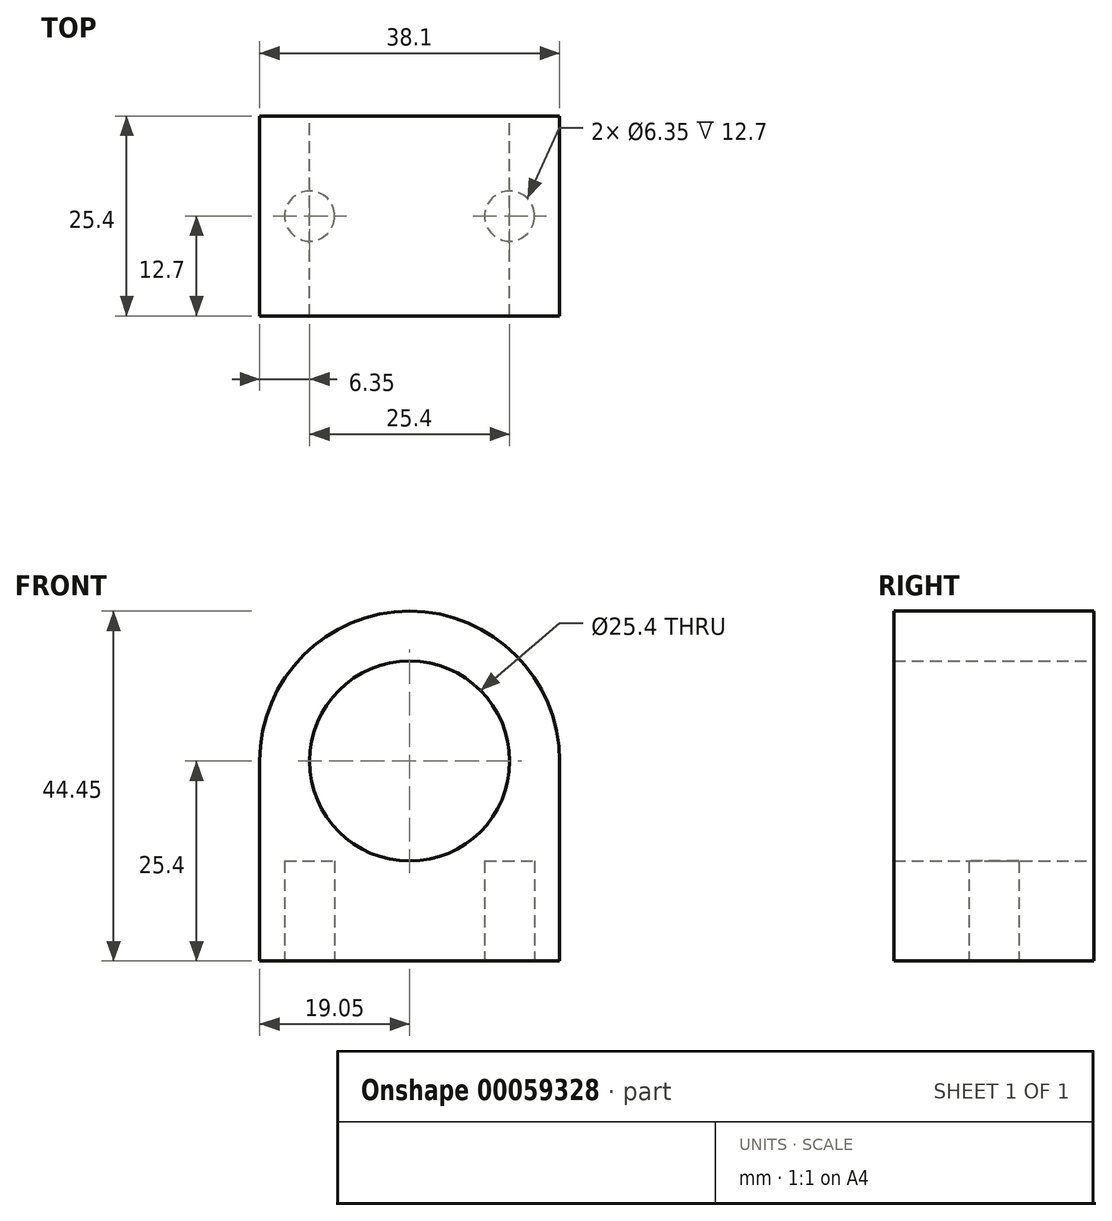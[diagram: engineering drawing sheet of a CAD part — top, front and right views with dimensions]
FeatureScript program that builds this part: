
annotation { "Feature Type Name" : "Feature", "Feature Type Description" : "" }
export const myFeature = defineFeature(function(context is Context, id is Id, definition is map)
    precondition{}
    {
        {
            var Q0;
            Q0=qCreatedBy(makeId("Front.planeOp"),FACE);
            var sketch = newSketch(context, id + "F0", { "sketchPlane" : qUnion([Q0])});
            skArc(sketch, "E0", {"start": v(19.05, 0) * mm, "mid": v(0, 19.05) * mm, "end": v(-19.05, 0) * mm});
            skLineSegment(sketch, "E1.top", {"start": v(-19.05, -25.4) * mm, "end": v(19.05, -25.4) * mm});
            skLineSegment(sketch, "E1.left", {"start": v(-19.05, 0) * mm, "end": v(-19.05, -25.4) * mm});
            skLineSegment(sketch, "E1.right", {"start": v(19.05, 0) * mm, "end": v(19.05, -25.4) * mm});
            skCircle(sketch, "E2", {"center": v(0, 0) * mm, "radius": 12.7 * mm});
            skSolve(sketch);
        }
        {
            var Q0;
            Q0=makeQuery(id+"F0.imprint","IMPRINT",FACE,{"disambiguationData":[TD([[makeQuery(id+"F0.imprint","IMPRINT",EDGE,{"derivedFrom":sQuery(id+"F0.wireOp",EDGE,"E0")}),1.0]])]});
            extrude(context, id + "F1", {"entities" : qUnion([Q0]), "depth" : 25.4 * mm});
        }
        {
            var Q0;
            Q0=makeQuery(id+"F1.opExtrude","SWEPT_FACE",FACE,{"disambiguationData":[OSD([sQuery(id+"F0.wireOp",EDGE,"E1.top")])]});
            var sketch = newSketch(context, id + "F2", { "sketchPlane" : qUnion([Q0])});
            skCircle(sketch, "E3", {"center": v(-12.7, 12.7) * mm, "radius": 3.18 * mm});
            skCircle(sketch, "E4", {"center": v(12.7, 12.7) * mm, "radius": 3.18 * mm});
            skSolve(sketch);
        }
        {
            var Q0;
            Q0=makeQuery(id+"F2.imprint","IMPRINT",FACE,{"disambiguationData":[TD([[makeQuery(id+"F2.imprint","IMPRINT",EDGE,{"derivedFrom":sQuery(id+"F2.wireOp",EDGE,"E3")}),1.0]])]});
            var Q1;
            Q1=makeQuery(id+"F2.imprint","IMPRINT",FACE,{"disambiguationData":[TD([[makeQuery(id+"F2.imprint","IMPRINT",EDGE,{"derivedFrom":sQuery(id+"F2.wireOp",EDGE,"E4")}),1.0]])]});
            extrude(context, id + "F3", {"entities" : qUnion([Q0, Q1]), "operationType" : NewBodyOperationType.REMOVE, "oppositeDirection" : true, "depth" : 12.7 * mm});
        }
    });
